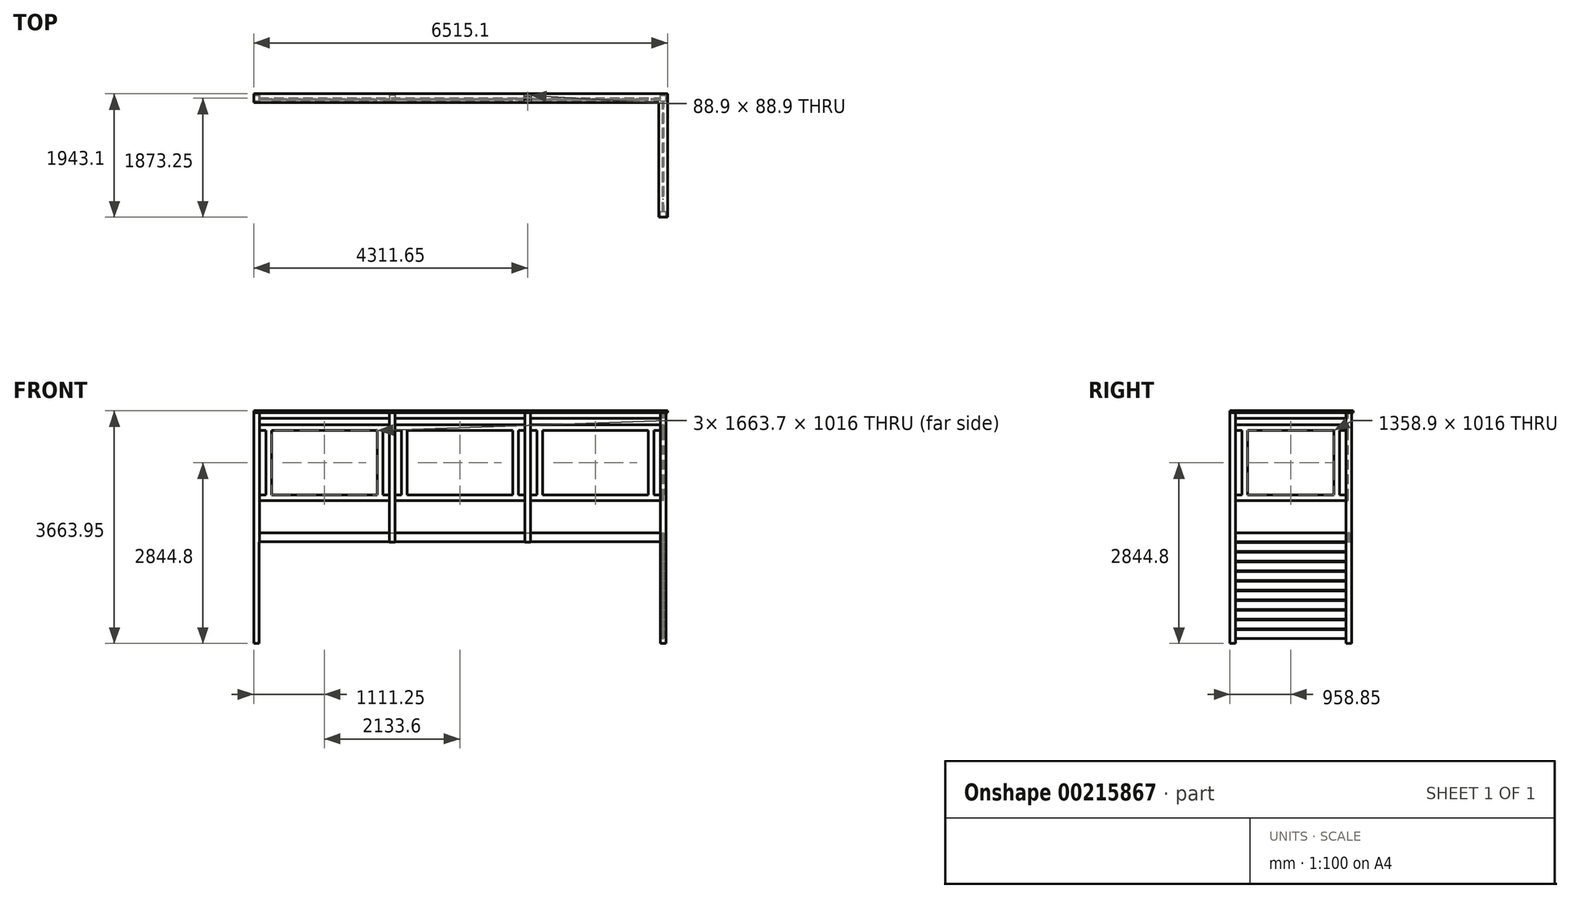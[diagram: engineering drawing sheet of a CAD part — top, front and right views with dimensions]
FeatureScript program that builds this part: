
annotation { "Feature Type Name" : "Feature", "Feature Type Description" : "" }
export const myFeature = defineFeature(function(context is Context, id is Id, definition is map)
    precondition{}
    {
        {
            var Q0;
            Q0=qCreatedBy(makeId("Top.planeOp"),FACE);
            var sketch = newSketch(context, id + "F0", { "sketchPlane" : qUnion([Q0])});
            skLineSegment(sketch, "E0", {"start": v(0, 0) * mm, "end": v(6400.8, 0) * mm, "construction": true});
            skLineSegment(sketch, "E1", {"start": v(6400.8, 0) * mm, "end": v(6400.8, -1828.8) * mm, "construction": true});
            skLineSegment(sketch, "E2.bottom", {"start": v(6400.8, 0) * mm, "end": v(6489.7, 0) * mm});
            skLineSegment(sketch, "E2.top", {"start": v(6400.8, 88.9) * mm, "end": v(6489.7, 88.9) * mm});
            skLineSegment(sketch, "E2.left", {"start": v(6400.8, 0) * mm, "end": v(6400.8, 88.9) * mm});
            skLineSegment(sketch, "E2.right", {"start": v(6489.7, 0) * mm, "end": v(6489.7, 88.9) * mm});
            skLineSegment(sketch, "E3.bottom", {"start": v(6400.8, -1828.8) * mm, "end": v(6489.7, -1828.8) * mm});
            skLineSegment(sketch, "E3.top", {"start": v(6400.8, -1739.9) * mm, "end": v(6489.7, -1739.9) * mm});
            skLineSegment(sketch, "E3.left", {"start": v(6400.8, -1828.8) * mm, "end": v(6400.8, -1739.9) * mm});
            skLineSegment(sketch, "E3.right", {"start": v(6489.7, -1828.8) * mm, "end": v(6489.7, -1739.9) * mm});
            skLineSegment(sketch, "E4.bottom", {"start": v(0, 0) * mm, "end": v(88.9, 0) * mm});
            skLineSegment(sketch, "E4.top", {"start": v(0, 88.9) * mm, "end": v(88.9, 88.9) * mm});
            skLineSegment(sketch, "E4.left", {"start": v(0, 0) * mm, "end": v(0, 88.9) * mm});
            skLineSegment(sketch, "E4.right", {"start": v(88.9, 0) * mm, "end": v(88.9, 88.9) * mm});
            skLineSegment(sketch, "E5.bottom", {"start": v(2133.6, 0) * mm, "end": v(2222.5, 0) * mm});
            skLineSegment(sketch, "E5.top", {"start": v(2133.6, 88.9) * mm, "end": v(2222.5, 88.9) * mm});
            skLineSegment(sketch, "E5.left", {"start": v(2133.6, 0) * mm, "end": v(2133.6, 88.9) * mm});
            skLineSegment(sketch, "E5.right", {"start": v(2222.5, 0) * mm, "end": v(2222.5, 88.9) * mm});
            skLineSegment(sketch, "E6.bottom", {"start": v(4267.2, 0) * mm, "end": v(4356.1, 0) * mm});
            skLineSegment(sketch, "E6.top", {"start": v(4267.2, 88.9) * mm, "end": v(4356.1, 88.9) * mm});
            skLineSegment(sketch, "E6.left", {"start": v(4267.2, 0) * mm, "end": v(4267.2, 88.9) * mm});
            skLineSegment(sketch, "E6.right", {"start": v(4356.1, 0) * mm, "end": v(4356.1, 88.9) * mm});
            skSolve(sketch);
        }
        {
            var Q0;
            Q0 = qSketchRegion(id + "F0", true);
            extrude(context, id + "F1", {"entities" : qUnion([Q0]), "depth" : 3632.2 * mm, "offsetDistance" : 25.4 * mm});
        }
        {
            var Q0;
            Q0=makeQuery(id+"F1.opExtrude","SWEPT_FACE",FACE,{"disambiguationData":[OSD([sQuery(id+"F0.wireOp",EDGE,"E2.bottom")])]});
            var sketch = newSketch(context, id + "F2", { "sketchPlane" : qUnion([Q0])});
            skLineSegment(sketch, "E7", {"start": v(6037.34, 1739.9) * mm, "end": v(6981.16, 1739.9) * mm, "construction": true});
            skLineSegment(sketch, "E8.bottom", {"start": v(6435.73, 1739.9) * mm, "end": v(6454.78, 1739.9) * mm});
            skLineSegment(sketch, "E8.top", {"start": v(6435.73, 1600.2) * mm, "end": v(6454.78, 1600.2) * mm});
            skLineSegment(sketch, "E8.left", {"start": v(6435.73, 1739.9) * mm, "end": v(6435.73, 1600.2) * mm});
            skLineSegment(sketch, "E8.right", {"start": v(6454.78, 1739.9) * mm, "end": v(6454.78, 1600.2) * mm});
            skLineSegment(sketch, "E9.bottom", {"start": v(6435.73, 1587.5) * mm, "end": v(6454.78, 1587.5) * mm});
            skLineSegment(sketch, "E9.top", {"start": v(6435.73, 1447.8) * mm, "end": v(6454.78, 1447.8) * mm});
            skLineSegment(sketch, "E9.left", {"start": v(6435.73, 1587.5) * mm, "end": v(6435.73, 1447.8) * mm});
            skLineSegment(sketch, "E9.right", {"start": v(6454.78, 1587.5) * mm, "end": v(6454.78, 1447.8) * mm});
            skLineSegment(sketch, "E10.bottom", {"start": v(6435.73, 1435.1) * mm, "end": v(6454.78, 1435.1) * mm});
            skLineSegment(sketch, "E10.top", {"start": v(6435.73, 1295.4) * mm, "end": v(6454.78, 1295.4) * mm});
            skLineSegment(sketch, "E10.left", {"start": v(6435.73, 1435.1) * mm, "end": v(6435.73, 1295.4) * mm});
            skLineSegment(sketch, "E10.right", {"start": v(6454.78, 1435.1) * mm, "end": v(6454.78, 1295.4) * mm});
            skLineSegment(sketch, "E11.bottom", {"start": v(6435.73, 1282.7) * mm, "end": v(6454.78, 1282.7) * mm});
            skLineSegment(sketch, "E11.top", {"start": v(6435.73, 1143) * mm, "end": v(6454.78, 1143) * mm});
            skLineSegment(sketch, "E11.left", {"start": v(6435.73, 1282.7) * mm, "end": v(6435.73, 1143) * mm});
            skLineSegment(sketch, "E11.right", {"start": v(6454.78, 1282.7) * mm, "end": v(6454.78, 1143) * mm});
            skLineSegment(sketch, "E12.bottom", {"start": v(6435.73, 1130.3) * mm, "end": v(6454.78, 1130.3) * mm});
            skLineSegment(sketch, "E12.top", {"start": v(6435.73, 990.6) * mm, "end": v(6454.78, 990.6) * mm});
            skLineSegment(sketch, "E12.left", {"start": v(6435.73, 1130.3) * mm, "end": v(6435.73, 990.6) * mm});
            skLineSegment(sketch, "E12.right", {"start": v(6454.78, 1130.3) * mm, "end": v(6454.78, 990.6) * mm});
            skLineSegment(sketch, "E13.bottom", {"start": v(6435.73, 977.9) * mm, "end": v(6454.78, 977.9) * mm});
            skLineSegment(sketch, "E13.top", {"start": v(6435.73, 838.2) * mm, "end": v(6454.78, 838.2) * mm});
            skLineSegment(sketch, "E13.left", {"start": v(6435.73, 977.9) * mm, "end": v(6435.73, 838.2) * mm});
            skLineSegment(sketch, "E13.right", {"start": v(6454.78, 977.9) * mm, "end": v(6454.78, 838.2) * mm});
            skLineSegment(sketch, "E14.bottom", {"start": v(6435.73, 825.5) * mm, "end": v(6454.78, 825.5) * mm});
            skLineSegment(sketch, "E14.top", {"start": v(6435.73, 685.8) * mm, "end": v(6454.78, 685.8) * mm});
            skLineSegment(sketch, "E14.left", {"start": v(6435.73, 825.5) * mm, "end": v(6435.73, 685.8) * mm});
            skLineSegment(sketch, "E14.right", {"start": v(6454.78, 825.5) * mm, "end": v(6454.78, 685.8) * mm});
            skLineSegment(sketch, "E15.bottom", {"start": v(6435.73, 673.1) * mm, "end": v(6454.78, 673.1) * mm});
            skLineSegment(sketch, "E15.top", {"start": v(6435.73, 533.4) * mm, "end": v(6454.78, 533.4) * mm});
            skLineSegment(sketch, "E15.left", {"start": v(6435.73, 673.1) * mm, "end": v(6435.73, 533.4) * mm});
            skLineSegment(sketch, "E15.right", {"start": v(6454.78, 673.1) * mm, "end": v(6454.78, 533.4) * mm});
            skLineSegment(sketch, "E16.bottom", {"start": v(6435.73, 520.7) * mm, "end": v(6454.78, 520.7) * mm});
            skLineSegment(sketch, "E16.top", {"start": v(6435.73, 381) * mm, "end": v(6454.78, 381) * mm});
            skLineSegment(sketch, "E16.left", {"start": v(6435.73, 520.7) * mm, "end": v(6435.73, 381) * mm});
            skLineSegment(sketch, "E16.right", {"start": v(6454.78, 520.7) * mm, "end": v(6454.78, 381) * mm});
            skLineSegment(sketch, "E17.bottom", {"start": v(6435.73, 368.3) * mm, "end": v(6454.78, 368.3) * mm});
            skLineSegment(sketch, "E17.top", {"start": v(6435.73, 228.6) * mm, "end": v(6454.78, 228.6) * mm});
            skLineSegment(sketch, "E17.left", {"start": v(6435.73, 368.3) * mm, "end": v(6435.73, 228.6) * mm});
            skLineSegment(sketch, "E17.right", {"start": v(6454.78, 368.3) * mm, "end": v(6454.78, 228.6) * mm});
            skLineSegment(sketch, "E18.bottom", {"start": v(6435.73, 215.9) * mm, "end": v(6454.78, 215.9) * mm});
            skLineSegment(sketch, "E18.top", {"start": v(6435.73, 76.2) * mm, "end": v(6454.78, 76.2) * mm});
            skLineSegment(sketch, "E18.left", {"start": v(6435.73, 215.9) * mm, "end": v(6435.73, 76.2) * mm});
            skLineSegment(sketch, "E18.right", {"start": v(6454.78, 215.9) * mm, "end": v(6454.78, 76.2) * mm});
            skSolve(sketch);
        }
        {
            var Q0;
            Q0 = qSketchRegion(id + "F2", true);
            extrude(context, id + "F3", {"entities" : qUnion([Q0]), "depth" : 1739.9 * mm});
        }
        {
            var Q0;
            Q0=makeQuery(id+"F1.opExtrude","SWEPT_FACE",FACE,{"disambiguationData":[OSD([sQuery(id+"F0.wireOp",EDGE,"E2.left")])]});
            var sketch = newSketch(context, id + "F4", { "sketchPlane" : qUnion([Q0])});
            skLineSegment(sketch, "E19.bottom", {"start": v(-53.97, 1739.9) * mm, "end": v(-34.92, 1739.9) * mm});
            skLineSegment(sketch, "E19.top", {"start": v(-53.97, 1600.2) * mm, "end": v(-34.92, 1600.2) * mm});
            skLineSegment(sketch, "E19.left", {"start": v(-53.97, 1739.9) * mm, "end": v(-53.97, 1600.2) * mm});
            skLineSegment(sketch, "E19.right", {"start": v(-34.92, 1739.9) * mm, "end": v(-34.92, 1600.2) * mm});
            skLineSegment(sketch, "E20.bottom", {"start": v(-53.97, 1587.5) * mm, "end": v(-34.92, 1587.5) * mm});
            skLineSegment(sketch, "E20.top", {"start": v(-53.97, 1447.8) * mm, "end": v(-34.92, 1447.8) * mm});
            skLineSegment(sketch, "E20.left", {"start": v(-53.97, 1587.5) * mm, "end": v(-53.97, 1447.8) * mm});
            skLineSegment(sketch, "E20.right", {"start": v(-34.92, 1587.5) * mm, "end": v(-34.92, 1447.8) * mm});
            skLineSegment(sketch, "E21.bottom", {"start": v(-53.97, 1435.1) * mm, "end": v(-34.92, 1435.1) * mm});
            skLineSegment(sketch, "E21.top", {"start": v(-53.97, 1295.4) * mm, "end": v(-34.92, 1295.4) * mm});
            skLineSegment(sketch, "E21.left", {"start": v(-53.97, 1435.1) * mm, "end": v(-53.97, 1295.4) * mm});
            skLineSegment(sketch, "E21.right", {"start": v(-34.92, 1435.1) * mm, "end": v(-34.92, 1295.4) * mm});
            skLineSegment(sketch, "E22.bottom", {"start": v(-53.97, 1282.7) * mm, "end": v(-34.92, 1282.7) * mm});
            skLineSegment(sketch, "E22.top", {"start": v(-53.97, 1143) * mm, "end": v(-34.92, 1143) * mm});
            skLineSegment(sketch, "E22.left", {"start": v(-53.97, 1282.7) * mm, "end": v(-53.97, 1143) * mm});
            skLineSegment(sketch, "E22.right", {"start": v(-34.92, 1282.7) * mm, "end": v(-34.92, 1143) * mm});
            skLineSegment(sketch, "E23.bottom", {"start": v(-53.97, 1130.3) * mm, "end": v(-34.92, 1130.3) * mm});
            skLineSegment(sketch, "E23.top", {"start": v(-53.97, 990.6) * mm, "end": v(-34.92, 990.6) * mm});
            skLineSegment(sketch, "E23.left", {"start": v(-53.97, 1130.3) * mm, "end": v(-53.97, 990.6) * mm});
            skLineSegment(sketch, "E23.right", {"start": v(-34.92, 1130.3) * mm, "end": v(-34.92, 990.6) * mm});
            skLineSegment(sketch, "E24.bottom", {"start": v(-53.97, 977.9) * mm, "end": v(-34.92, 977.9) * mm});
            skLineSegment(sketch, "E24.top", {"start": v(-53.97, 838.2) * mm, "end": v(-34.92, 838.2) * mm});
            skLineSegment(sketch, "E24.left", {"start": v(-53.97, 977.9) * mm, "end": v(-53.97, 838.2) * mm});
            skLineSegment(sketch, "E24.right", {"start": v(-34.92, 977.9) * mm, "end": v(-34.92, 838.2) * mm});
            skLineSegment(sketch, "E25.bottom", {"start": v(-53.97, 825.5) * mm, "end": v(-34.92, 825.5) * mm});
            skLineSegment(sketch, "E25.top", {"start": v(-53.97, 685.8) * mm, "end": v(-34.92, 685.8) * mm});
            skLineSegment(sketch, "E25.left", {"start": v(-53.97, 825.5) * mm, "end": v(-53.97, 685.8) * mm});
            skLineSegment(sketch, "E25.right", {"start": v(-34.92, 825.5) * mm, "end": v(-34.92, 685.8) * mm});
            skLineSegment(sketch, "E26.bottom", {"start": v(-53.97, 673.1) * mm, "end": v(-34.92, 673.1) * mm});
            skLineSegment(sketch, "E26.top", {"start": v(-53.97, 533.4) * mm, "end": v(-34.92, 533.4) * mm});
            skLineSegment(sketch, "E26.left", {"start": v(-53.97, 673.1) * mm, "end": v(-53.97, 533.4) * mm});
            skLineSegment(sketch, "E26.right", {"start": v(-34.92, 673.1) * mm, "end": v(-34.92, 533.4) * mm});
            skLineSegment(sketch, "E27.bottom", {"start": v(-53.97, 520.7) * mm, "end": v(-34.92, 520.7) * mm});
            skLineSegment(sketch, "E27.top", {"start": v(-53.97, 381) * mm, "end": v(-34.92, 381) * mm});
            skLineSegment(sketch, "E27.left", {"start": v(-53.97, 520.7) * mm, "end": v(-53.97, 381) * mm});
            skLineSegment(sketch, "E27.right", {"start": v(-34.92, 520.7) * mm, "end": v(-34.92, 381) * mm});
            skPoint(sketch, "E28.firstSnap0", {"position": v(-53.97, 755.65) * mm});
            skLineSegment(sketch, "E28.bottom", {"start": v(-53.97, 368.3) * mm, "end": v(-34.92, 368.3) * mm});
            skLineSegment(sketch, "E28.top", {"start": v(-53.97, 228.6) * mm, "end": v(-34.92, 228.6) * mm});
            skLineSegment(sketch, "E28.left", {"start": v(-53.97, 368.3) * mm, "end": v(-53.97, 228.6) * mm});
            skLineSegment(sketch, "E28.right", {"start": v(-34.92, 368.3) * mm, "end": v(-34.92, 228.6) * mm});
            skLineSegment(sketch, "E29.bottom", {"start": v(-53.97, 215.9) * mm, "end": v(-34.92, 215.9) * mm});
            skLineSegment(sketch, "E29.top", {"start": v(-53.97, 76.2) * mm, "end": v(-34.92, 76.2) * mm});
            skLineSegment(sketch, "E29.left", {"start": v(-53.97, 215.9) * mm, "end": v(-53.97, 76.2) * mm});
            skLineSegment(sketch, "E29.right", {"start": v(-34.92, 215.9) * mm, "end": v(-34.92, 76.2) * mm});
            skSolve(sketch);
        }
        {
            var Q0;
            Q0 = qSketchRegion(id + "F4", true);
            extrude(context, id + "F5", {"entities" : qUnion([Q0]), "depth" : 6311.9 * mm});
        }
        {
            var Q0;
            Q0=makeQuery(id+"F1.opExtrude","CAP_FACE",FACE,{"disambiguationData":[OSD([sQuery(id+"F0.wireOp",EDGE,"E6.bottom"),sQuery(id+"F0.wireOp",EDGE,"E6.top"),sQuery(id+"F0.wireOp",EDGE,"E6.left"),sQuery(id+"F0.wireOp",EDGE,"E6.right")])],"isStart":false});
            var sketch = newSketch(context, id + "F6", { "sketchPlane" : qUnion([Q0])});
            skLineSegment(sketch, "E30.bottom", {"start": v(0, -25.4) * mm, "end": v(6375.4, -25.4) * mm});
            skLineSegment(sketch, "E30.top", {"start": v(0, 114.3) * mm, "end": v(6515.1, 114.3) * mm});
            skLineSegment(sketch, "E30.left", {"start": v(0, -25.4) * mm, "end": v(0, 114.3) * mm});
            skLineSegment(sketch, "E31.bottom", {"start": v(6375.4, -1828.8) * mm, "end": v(6515.1, -1828.8) * mm});
            skLineSegment(sketch, "E31.left", {"start": v(6375.4, -1828.8) * mm, "end": v(6375.4, -25.4) * mm});
            skLineSegment(sketch, "E31.right", {"start": v(6515.1, -1828.8) * mm, "end": v(6515.1, 114.3) * mm});
            skSolve(sketch);
        }
        {
            var Q0;
            Q0=makeQuery(id+"F6.imprint","IMPRINT",FACE,{"disambiguationData":[TD([[makeQuery(id+"F6.imprint","IMPRINT",EDGE,{"derivedFrom":sQuery(id+"F6.wireOp",EDGE,"E30.bottom")}),1.0]])]});
            extrude(context, id + "F7", {"entities" : qUnion([Q0]), "depth" : 31.75 * mm});
        }
        {
            var Q0;
            Q0=makeQuery(id+"F3.opExtrude","SWEPT_FACE",FACE,{"disambiguationData":[OSD([sQuery(id+"F2.wireOp",EDGE,"E8.left")])]});
            var sketch = newSketch(context, id + "F8", { "sketchPlane" : qUnion([Q0])});
            skLineSegment(sketch, "E32.bottom", {"start": v(0, 3632.2) * mm, "end": v(1739.9, 3632.2) * mm});
            skLineSegment(sketch, "E32.top", {"start": v(0, 3543.3) * mm, "end": v(1739.9, 3543.3) * mm});
            skLineSegment(sketch, "E32.left", {"start": v(0, 3632.2) * mm, "end": v(0, 3543.3) * mm});
            skLineSegment(sketch, "E32.right", {"start": v(1739.9, 3632.2) * mm, "end": v(1739.9, 3543.3) * mm});
            skLineSegment(sketch, "E33.bottom", {"start": v(0, 3441.7) * mm, "end": v(1739.9, 3441.7) * mm});
            skLineSegment(sketch, "E33.top", {"start": v(0, 3352.8) * mm, "end": v(101.6, 3352.8) * mm});
            skLineSegment(sketch, "E33.left", {"start": v(0, 3441.7) * mm, "end": v(0, 3352.8) * mm});
            skLineSegment(sketch, "E33.right", {"start": v(1739.9, 3441.7) * mm, "end": v(1739.9, 3352.8) * mm});
            skLineSegment(sketch, "E34.bottom", {"start": v(0, 2247.9) * mm, "end": v(1739.9, 2247.9) * mm});
            skLineSegment(sketch, "E34.top", {"start": v(0, 2336.8) * mm, "end": v(101.6, 2336.8) * mm});
            skLineSegment(sketch, "E34.left", {"start": v(0, 2247.9) * mm, "end": v(0, 2336.8) * mm});
            skLineSegment(sketch, "E34.right", {"start": v(1739.9, 2247.9) * mm, "end": v(1739.9, 2336.8) * mm});
            skLineSegment(sketch, "E35.left", {"start": v(101.6, 3352.8) * mm, "end": v(101.6, 2336.8) * mm});
            skLineSegment(sketch, "E35.right", {"start": v(190.5, 3352.8) * mm, "end": v(190.5, 2336.8) * mm});
            skLineSegment(sketch, "E36.left", {"start": v(1549.4, 3352.8) * mm, "end": v(1549.4, 2336.8) * mm});
            skLineSegment(sketch, "E36.right", {"start": v(1638.3, 3352.8) * mm, "end": v(1638.3, 2336.8) * mm});
            skLineSegment(sketch, "E37.trimOffspring", {"start": v(1638.3, 3352.8) * mm, "end": v(1739.9, 3352.8) * mm});
            skLineSegment(sketch, "E38.trimOffspring", {"start": v(1638.3, 2336.8) * mm, "end": v(1739.9, 2336.8) * mm});
            skLineSegment(sketch, "E39.trimOffspring", {"start": v(190.5, 2336.8) * mm, "end": v(1549.4, 2336.8) * mm});
            skLineSegment(sketch, "E40.trimOffspring", {"start": v(190.5, 3352.8) * mm, "end": v(1549.4, 3352.8) * mm});
            skSolve(sketch);
        }
        {
            var Q0;
            Q0 = qSketchRegion(id + "F8", true);
            extrude(context, id + "F9", {"entities" : qUnion([Q0]), "oppositeDirection" : true, "depth" : 19.05 * mm});
        }
        {
            var Q0;
            Q0=makeQuery(id+"F5.opExtrude","SWEPT_FACE",FACE,{"disambiguationData":[OSD([sQuery(id+"F4.wireOp",EDGE,"E19.right")])]});
            var sketch = newSketch(context, id + "F10", { "sketchPlane" : qUnion([Q0])});
            skLineSegment(sketch, "E41.bottom", {"start": v(6400.8, 3632.2) * mm, "end": v(4356.1, 3632.2) * mm});
            skLineSegment(sketch, "E41.top", {"start": v(6400.8, 3543.3) * mm, "end": v(4356.1, 3543.3) * mm});
            skLineSegment(sketch, "E41.left", {"start": v(6400.8, 3632.2) * mm, "end": v(6400.8, 3543.3) * mm});
            skLineSegment(sketch, "E41.right", {"start": v(4356.1, 3632.2) * mm, "end": v(4356.1, 3543.3) * mm});
            skLineSegment(sketch, "E42.bottom", {"start": v(4267.2, 3632.2) * mm, "end": v(2222.5, 3632.2) * mm});
            skLineSegment(sketch, "E42.top", {"start": v(4267.2, 3543.3) * mm, "end": v(2222.5, 3543.3) * mm});
            skLineSegment(sketch, "E42.left", {"start": v(4267.2, 3632.2) * mm, "end": v(4267.2, 3543.3) * mm});
            skLineSegment(sketch, "E42.right", {"start": v(2222.5, 3632.2) * mm, "end": v(2222.5, 3543.3) * mm});
            skLineSegment(sketch, "E43.bottom", {"start": v(2133.6, 3632.2) * mm, "end": v(88.9, 3632.2) * mm});
            skLineSegment(sketch, "E43.top", {"start": v(2133.6, 3543.3) * mm, "end": v(88.9, 3543.3) * mm});
            skLineSegment(sketch, "E43.left", {"start": v(2133.6, 3632.2) * mm, "end": v(2133.6, 3543.3) * mm});
            skLineSegment(sketch, "E43.right", {"start": v(88.9, 3632.2) * mm, "end": v(88.9, 3543.3) * mm});
            skLineSegment(sketch, "E44.bottom", {"start": v(6400.8, 3441.7) * mm, "end": v(4356.1, 3441.7) * mm});
            skLineSegment(sketch, "E44.top", {"start": v(6400.8, 3352.8) * mm, "end": v(6299.2, 3352.8) * mm});
            skLineSegment(sketch, "E44.left", {"start": v(6400.8, 3441.7) * mm, "end": v(6400.8, 3352.8) * mm});
            skLineSegment(sketch, "E44.right", {"start": v(4356.1, 3441.7) * mm, "end": v(4356.1, 3352.8) * mm});
            skLineSegment(sketch, "E45.bottom", {"start": v(4267.2, 3441.7) * mm, "end": v(2222.5, 3441.7) * mm});
            skLineSegment(sketch, "E45.top", {"start": v(4267.2, 3352.8) * mm, "end": v(4165.6, 3352.8) * mm});
            skLineSegment(sketch, "E45.left", {"start": v(4267.2, 3441.7) * mm, "end": v(4267.2, 3352.8) * mm});
            skLineSegment(sketch, "E45.right", {"start": v(2222.5, 3441.7) * mm, "end": v(2222.5, 3352.8) * mm});
            skLineSegment(sketch, "E46.bottom", {"start": v(2133.6, 3441.7) * mm, "end": v(88.9, 3441.7) * mm});
            skLineSegment(sketch, "E46.top", {"start": v(2133.6, 3352.8) * mm, "end": v(2032, 3352.8) * mm});
            skLineSegment(sketch, "E46.left", {"start": v(2133.6, 3441.7) * mm, "end": v(2133.6, 3352.8) * mm});
            skLineSegment(sketch, "E46.right", {"start": v(88.9, 3441.7) * mm, "end": v(88.9, 3352.8) * mm});
            skLineSegment(sketch, "E47.bottom", {"start": v(88.9, 2336.8) * mm, "end": v(190.5, 2336.8) * mm});
            skLineSegment(sketch, "E47.top", {"start": v(88.9, 2247.9) * mm, "end": v(2133.6, 2247.9) * mm});
            skLineSegment(sketch, "E47.left", {"start": v(88.9, 2336.8) * mm, "end": v(88.9, 2247.9) * mm});
            skLineSegment(sketch, "E47.right", {"start": v(2133.6, 2336.8) * mm, "end": v(2133.6, 2247.9) * mm});
            skLineSegment(sketch, "E48.bottom", {"start": v(2222.5, 2336.8) * mm, "end": v(2324.1, 2336.8) * mm});
            skLineSegment(sketch, "E48.top", {"start": v(2222.5, 2247.9) * mm, "end": v(4267.2, 2247.9) * mm});
            skLineSegment(sketch, "E48.left", {"start": v(2222.5, 2336.8) * mm, "end": v(2222.5, 2247.9) * mm});
            skLineSegment(sketch, "E48.right", {"start": v(4267.2, 2336.8) * mm, "end": v(4267.2, 2247.9) * mm});
            skLineSegment(sketch, "E49.bottom", {"start": v(4356.1, 2336.8) * mm, "end": v(4457.7, 2336.8) * mm});
            skLineSegment(sketch, "E49.top", {"start": v(4356.1, 2247.9) * mm, "end": v(6400.8, 2247.9) * mm});
            skLineSegment(sketch, "E49.left", {"start": v(4356.1, 2336.8) * mm, "end": v(4356.1, 2247.9) * mm});
            skLineSegment(sketch, "E49.right", {"start": v(6400.8, 2336.8) * mm, "end": v(6400.8, 2247.9) * mm});
            skLineSegment(sketch, "E50.left", {"start": v(6299.2, 3352.8) * mm, "end": v(6299.2, 2336.8) * mm});
            skLineSegment(sketch, "E50.right", {"start": v(6210.3, 3352.8) * mm, "end": v(6210.3, 2336.8) * mm});
            skLineSegment(sketch, "E51.left", {"start": v(4546.6, 3352.8) * mm, "end": v(4546.6, 2336.8) * mm});
            skLineSegment(sketch, "E51.right", {"start": v(4457.7, 3352.8) * mm, "end": v(4457.7, 2336.8) * mm});
            skLineSegment(sketch, "E52.left", {"start": v(4165.6, 3352.8) * mm, "end": v(4165.6, 2336.8) * mm});
            skLineSegment(sketch, "E52.right", {"start": v(4076.7, 3352.8) * mm, "end": v(4076.7, 2336.8) * mm});
            skLineSegment(sketch, "E53.left", {"start": v(2324.1, 3352.8) * mm, "end": v(2324.1, 2336.8) * mm});
            skLineSegment(sketch, "E53.right", {"start": v(2413, 3352.8) * mm, "end": v(2413, 2336.8) * mm});
            skLineSegment(sketch, "E54.left", {"start": v(2032, 3352.8) * mm, "end": v(2032, 2336.8) * mm});
            skLineSegment(sketch, "E54.right", {"start": v(1943.1, 3352.8) * mm, "end": v(1943.1, 2336.8) * mm});
            skLineSegment(sketch, "E55.left", {"start": v(279.4, 3352.8) * mm, "end": v(279.4, 2336.8) * mm});
            skLineSegment(sketch, "E55.right", {"start": v(190.5, 3352.8) * mm, "end": v(190.5, 2336.8) * mm});
            skLineSegment(sketch, "E56.trimOffspring", {"start": v(190.5, 3352.8) * mm, "end": v(88.9, 3352.8) * mm});
            skLineSegment(sketch, "E57.trimOffspring", {"start": v(279.4, 2336.8) * mm, "end": v(1943.1, 2336.8) * mm});
            skLineSegment(sketch, "E58.trimOffspring", {"start": v(1943.1, 3352.8) * mm, "end": v(279.4, 3352.8) * mm});
            skLineSegment(sketch, "E59.trimOffspring", {"start": v(2032, 2336.8) * mm, "end": v(2133.6, 2336.8) * mm});
            skLineSegment(sketch, "E60.trimOffspring", {"start": v(2324.1, 3352.8) * mm, "end": v(2222.5, 3352.8) * mm});
            skLineSegment(sketch, "E61.trimOffspring", {"start": v(2413, 2336.8) * mm, "end": v(4076.7, 2336.8) * mm});
            skLineSegment(sketch, "E62.trimOffspring", {"start": v(4076.7, 3352.8) * mm, "end": v(2413, 3352.8) * mm});
            skLineSegment(sketch, "E63.trimOffspring", {"start": v(4165.6, 2336.8) * mm, "end": v(4267.2, 2336.8) * mm});
            skLineSegment(sketch, "E64.trimOffspring", {"start": v(4546.6, 2336.8) * mm, "end": v(6210.3, 2336.8) * mm});
            skLineSegment(sketch, "E65.trimOffspring", {"start": v(4457.7, 3352.8) * mm, "end": v(4356.1, 3352.8) * mm});
            skLineSegment(sketch, "E66.trimOffspring", {"start": v(6210.3, 3352.8) * mm, "end": v(4546.6, 3352.8) * mm});
            skLineSegment(sketch, "E67.trimOffspring", {"start": v(6299.2, 2336.8) * mm, "end": v(6400.8, 2336.8) * mm});
            skSolve(sketch);
        }
        {
            var Q0;
            Q0 = qSketchRegion(id + "F10", true);
            extrude(context, id + "F11", {"entities" : qUnion([Q0]), "depth" : 19.05 * mm});
        }
        {
            var Q0;
            Q0=makeQuery(id+"F1.opExtrude","SWEPT_FACE",FACE,{"disambiguationData":[OSD([sQuery(id+"F0.wireOp",EDGE,"E2.top")])]});
            var sketch = newSketch(context, id + "F12", { "sketchPlane" : qUnion([Q0])});
            skLineSegment(sketch, "E68.bottom", {"start": v(-6400.8, 0) * mm, "end": v(-84.64, 0) * mm});
            skLineSegment(sketch, "E68.top", {"start": v(-6400.8, 1596.01) * mm, "end": v(-84.64, 1596.01) * mm});
            skLineSegment(sketch, "E68.left", {"start": v(-6400.8, 0) * mm, "end": v(-6400.8, 1596.01) * mm});
            skLineSegment(sketch, "E68.right", {"start": v(-84.64, 0) * mm, "end": v(-84.64, 1596.01) * mm});
            skSolve(sketch);
        }
        {
            var Q0;
            Q0=makeQuery(id+"F12.imprint","IMPRINT",FACE,{"disambiguationData":[TD([[makeQuery(id+"F12.imprint","IMPRINT",EDGE,{"derivedFrom":sQuery(id+"F12.wireOp",EDGE,"E68.bottom")}),1.0]])]});
            extrude(context, id + "F13", {"entities" : qUnion([Q0]), "operationType" : NewBodyOperationType.REMOVE, "oppositeDirection" : true, "depth" : 152.4 * mm});
        }
    });
